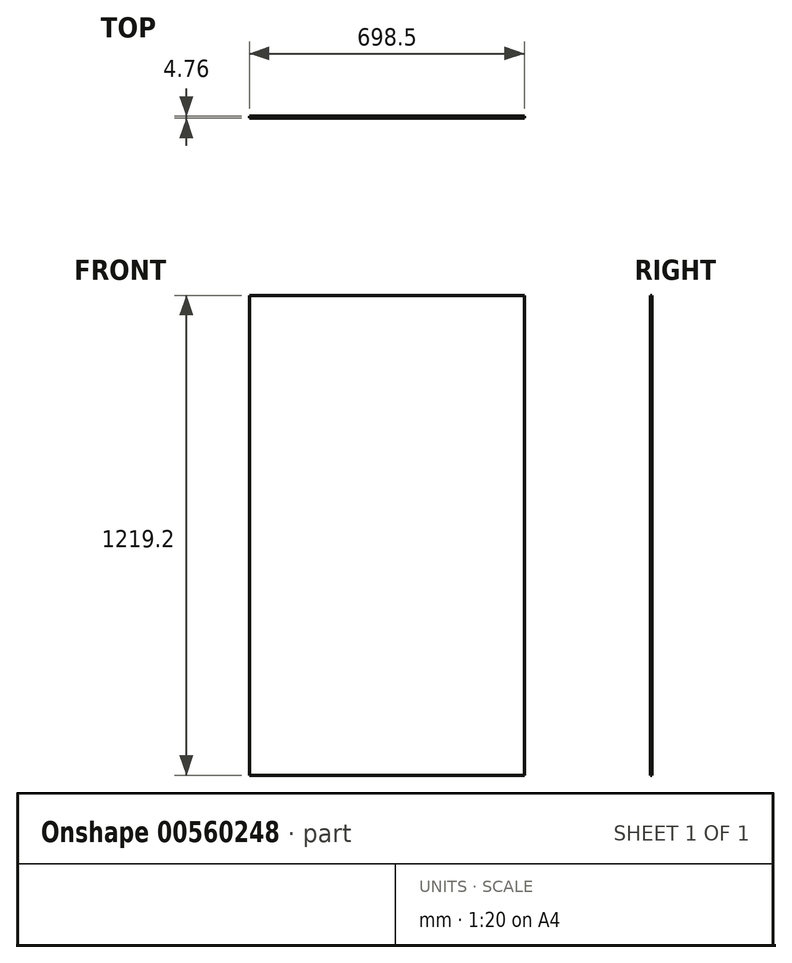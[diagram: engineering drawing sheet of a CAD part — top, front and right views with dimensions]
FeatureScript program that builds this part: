
annotation { "Feature Type Name" : "Feature", "Feature Type Description" : "" }
export const myFeature = defineFeature(function(context is Context, id is Id, definition is map)
    precondition{}
    {
        {
            var Q0;
            Q0=qCreatedBy(makeId("Front.planeOp"),FACE);
            var sketch = newSketch(context, id + "F0", { "sketchPlane" : qUnion([Q0])});
            skLineSegment(sketch, "E0.bottom", {"start": v(-349.25, 609.6) * mm, "end": v(349.25, 609.6) * mm});
            skLineSegment(sketch, "E0.top", {"start": v(-349.25, -609.6) * mm, "end": v(349.25, -609.6) * mm});
            skLineSegment(sketch, "E0.left", {"start": v(-349.25, 609.6) * mm, "end": v(-349.25, -609.6) * mm});
            skLineSegment(sketch, "E0.right", {"start": v(349.25, 609.6) * mm, "end": v(349.25, -609.6) * mm});
            skSolve(sketch);
        }
        {
            var Q0;
            Q0=makeQuery(id+"F0.imprint","IMPRINT",FACE,{"disambiguationData":[TD([[makeQuery(id+"F0.imprint","IMPRINT",EDGE,{"derivedFrom":sQuery(id+"F0.wireOp",EDGE,"E0.bottom")}),-1.0]])]});
            extrude(context, id + "F1", {"entities" : qUnion([Q0]), "endBound" : BoundingType.SYMMETRIC, "depth" : 4.76 * mm, "offsetDistance" : 25.4 * mm});
        }
    });
